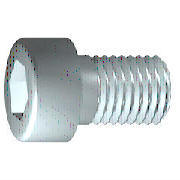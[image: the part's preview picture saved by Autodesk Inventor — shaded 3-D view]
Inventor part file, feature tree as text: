
AUTODESK INVENTOR PART (.ipt)
format: ipt  version: 2021 (Build 250183000, 183)  size: 187,392 bytes
history: native  units: mm (DEFAULTED — no unit token found)
features: sketch x2, extrude x1, plane x1, fillet x1
ambient origin geometry x7: Origin, YZ Plane, XY Plane, X Axis, Y Axis, Z Axis, Center Point
bodies: Solid1 (feature_tree), Body (feature_tree)
feature tree (5):
  extrude  "Slot"  Depth=2.5mm
  plane  "Work Plane1"
  fillet  "Fillet2"  Radius=2.5mm
  sketch  "Sketch1"  dims[d1=14.875mm d2=0.276153mm d3=2.5mm]
  sketch  "Sketch2"  dims[d4=1.1mm d5=60.0deg d6=2.5mm d7=2.5mm d8=2.309401mm d9=4.5mm d10=90.0deg d11=10.0mm d12=0.0mm d13=14.875mm d14=0.0mm d15=0.276052mm d16=0.276053mm d17=0.25mm d19=0.0mm d26=16.0mm d27=45.0deg d28=0.0mm d29=0.0mm d30=0.1mm]
